# Revit family: EKF_EE_ВерхняяПанельTrivia_AVERES
name_source: partatom
category: Электрооборудование
units: mm (PartAtom-declared; Revit-internal decimal feet)

## family parameters
Всегда вертикально = Нет
На основе рабочей плоскости = Да
Общий = Да
При загрузке вырезать с полостями = Нет
Размер круглого соединителя = Использовать диаметр
Тип детали = Силовой щит
Точка расчета площади = Нет

## types (24) — shared parameters
ADSK_Единица измерения = шт.
ADSK_Завод-изготовитель = EKF
ADSK_Количество = 1
ADSK_Марка = Верхняя панель
ADSK_Материал = RAL 7035_Сталь
ADSK_Обозначение = Верхняя панель
ADSK_Размер_Высота = 22 мм
t = 1.5 мм
Изготовитель = EKF
Креп1 = 29.5 мм
Креп2 = 51.3 мм
Отметка по умолчанию = 1219.2 мм
Отс1 = 44.5 мм
Отс2 = 50 мм
Серия номенклатуры = Averes
ТВ = EKF_2_TRIVIA_AVERES
Тип установки = -
zero-valued in all types: ADSK_Масса

## per-type parameters (varying)
| type | ADSK_Код изделия | ADSK_Наименование | ADSK_Размер_Глубина | ADSK_Размер_Ширина | IP55 | РымБолт_Глубина | РымБолт_Ширина | Степень защиты IP | Тип |
| Верхняя панель Ш300 Г400 EKF AVERES | PT3D400 | Верхняя панель Ш300 Г400 IP30 EKF AVERES | 415 мм | 309 мм | Нет | 312.4 мм | 250 мм | IP30 | 425 мм |
| Верхняя панель Ш300 Г400 IP55 EKF AVERES | PT3D400WP | Верхняя панель Ш300 Г400 IP55 EKF AVERES | 415 мм | 309 мм | Да | 312.4 мм | 250 мм | IP55 | 426 мм |
| Верхняя панель Ш300 Г600 EKF AVERES | PT3D600 | Верхняя панель Ш300 Г600 IP55 EKF AVERES | 615 мм | 309 мм | Да | 512.4 мм | 250 мм | IP55 | 427 мм |
| Верхняя панель Ш300 Г600 IP55 EKF AVERES | PT3D600WP | Верхняя панель Ш300 Г600 IP30 EKF AVERES | 615 мм | 309 мм | Да | 512.4 мм | 250 мм | IP30 | 428 мм |
| Верхняя панель Ш300 Г800 EKF AVERES | PT3D800 | Верхняя панель Ш300 Г800 IP30 EKF AVERES | 815 мм | 309 мм | Да | 712.4 мм | 250 мм | IP30 | 429 мм |
| Верхняя панель Ш300 Г800 IP55 EKF AVERES | PT3D800WP | Верхняя панель Ш300 Г800 IP55 EKF AVERES | 815 мм | 309 мм | Да | 712.4 мм | 250 мм | IP55 | 430 мм |
| Верхняя панель Ш400 Г400 EKF AVERES | PT4D400 | Верхняя панель Ш400 Г400 IP30 EKF AVERES | 415 мм | 409 мм | Да | 312.4 мм | 350 мм | IP30 | 431 мм |
| Верхняя панель Ш400 Г400 IP55 EKF AVERES | PT4D400WP | Верхняя панель Ш400 Г400 IP55 EKF AVERES | 415 мм | 409 мм | Да | 312.4 мм | 350 мм | IP55 | 432 мм |
| Верхняя панель Ш400 Г600 EKF AVERES | PT4D600 | Верхняя панель Ш400 Г600 IP30 EKF AVERES | 615 мм | 409 мм | Да | 512.4 мм | 350 мм | IP30 | 433 мм |
| Верхняя панель Ш400 Г600 IP55 EKF AVERES | PT4D600WP | Верхняя панель Ш400 Г600 IP55 EKF AVERES | 615 мм | 409 мм | Да | 512.4 мм | 350 мм | IP55 | 434 мм |
| Верхняя панель Ш400 Г800 EKF AVERES | PT4D800 | Верхняя панель Ш400 Г800 IP30 EKF AVERES | 815 мм | 409 мм | Да | 712.4 мм | 350 мм | IP30 | 435 мм |
| Верхняя панель Ш400 Г800 IP55 EKF AVERES | PT4D800WP | Верхняя панель Ш400 Г800 IP55 EKF AVERES | 815 мм | 409 мм | Да | 712.4 мм | 350 мм | IP55 | 436 мм |
| Верхняя панель Ш600 Г400 EKF AVERES | PT6D400 | Верхняя панель Ш600 Г400 IP55 EKF AVERES | 415 мм | 609 мм | Да | 312.4 мм | 550 мм | IP55 | 437 мм |
| Верхняя панель Ш600 Г400 IP55 EKF AVERES | PT6D400WP | Верхняя панель Ш600 Г400 IP30 EKF AVERES | 415 мм | 609 мм | Да | 312.4 мм | 550 мм | IP30 | 438 мм |
| Верхняя панель Ш600 Г600 EKF AVERES | PT6D600 | Верхняя панель Ш600 Г600 IP30 EKF AVERES | 615 мм | 609 мм | Да | 512.4 мм | 550 мм | IP30 | 439 мм |
| Верхняя панель Ш600 Г600 IP55 EKF AVERES | PT6D600WP | Верхняя панель Ш600 Г600 IP55 EKF AVERES | 615 мм | 609 мм | Да | 512.4 мм | 550 мм | IP55 | 440 мм |
| Верхняя панель Ш600 Г800 EKF AVERES | PT6D800 | Верхняя панель Ш600 Г800 IP30 EKF AVERES | 815 мм | 609 мм | Да | 712.4 мм | 550 мм | IP30 | 441 мм |
| Верхняя панель Ш600 Г800 IP55 EKF AVERES | PT6D800WP | Верхняя панель Ш600 Г800 IP55 EKF AVERES | 815 мм | 609 мм | Да | 712.4 мм | 550 мм | IP55 | 442 мм |
| Верхняя панель Ш800 Г400 EKF AVERES | PT8D400 | Верхняя панель Ш800 Г400 IP30 EKF AVERES | 415 мм | 809 мм | Да | 312.4 мм | 750 мм | IP30 | 443 мм |
| Верхняя панель Ш800 Г400 IP55 EKF AVERES | PT8D400WP | Верхняя панель Ш800 Г400 IP55 EKF AVERES | 415 мм | 809 мм | Да | 312.4 мм | 750 мм | IP55 | 444 мм |
| Верхняя панель Ш800 Г600 EKF AVERES | PT8D600 | Верхняя панель Ш800 Г600 IP30 EKF AVERES | 615 мм | 809 мм | Да | 512.4 мм | 750 мм | IP30 | 445 мм |
| Верхняя панель Ш800 Г600 IP55 EKF AVERES | PT8D600WP | Верхняя панель Ш800 Г600 IP55 EKF AVERES | 615 мм | 809 мм | Да | 512.4 мм | 750 мм | IP55 | 446 мм |
| Верхняя панель Ш800 Г800 EKF AVERES | PT8D800 | Верхняя панель Ш800 Г800 IP55 EKF AVERES | 815 мм | 809 мм | Да | 712.4 мм | 750 мм | IP55 | 447 мм |
| Верхняя панель Ш800 Г800 IP55 EKF AVERES | PT8D800WP | Верхняя панель Ш800 Г800 IP30 EKF AVERES | 815 мм | 809 мм | Да | 712.4 мм | 750 мм | IP30 | 448 мм |
